# Revit family: 7259 OSCA LEDxxxx
name_source: partatom
category: Lighting Fixtures
revit_build: Autodesk Revit LT 2014 (Build: 20130308_1515(x64)
units: mm (PartAtom-declared; Revit-internal decimal feet)

## types (1)
- 7259 Osca LED Round
    Apparent Load = 12 VA
    Assembly Code = D5020200
    Casing Material = Astro - Aluminium - Matt White
    Class = 1
    Color Filter = 16777215
    Default Elevation = 1219.2 mm  [stored 4 ft]
    Description = Downlight
    Dimmable = No
    Dimming Lamp Color Temperature Shift = <None>
    Height = 80 mm  [stored 0.262467 ft]
    IP Rating = IP20
    Lamp = LED
    Lamp included = Yes
    Length = 80 mm  [stored 0.262467 ft]
    Light Source Elevation = 47 mm  [stored 0.154199 ft]
    Manufacturer = Astro Lighting Ltd, CM20 2DP
    Model = 7259 Osca LED Round
    Mountable on normally flammable surfaces = Yes
    Number of Poles = 1
    Photometric Web File = 7259 OSCA LED ROUND.ies
    Product Documentation = http://www.astrolighting.co.uk
    Suitable for bathroom zone = Zone 3
    Tilt Angle = 0.00°
    Type Comments = Includes integral LED driver. Leading edge dimming.
    URL = www.astrolighting.co.uk
    Voltage = 230 V
    Wattage Comments = 12w
    Weight = 0.48kg
    Width = 80 mm  [stored 0.262467 ft]

note: [stored X ft] marks values corroborated as IEEE doubles in the binary element streams (Revit-internal decimal feet)

## geometry (parser evidence)
native form markers: Sweep x1
no freeform markers — native parametric forms only
